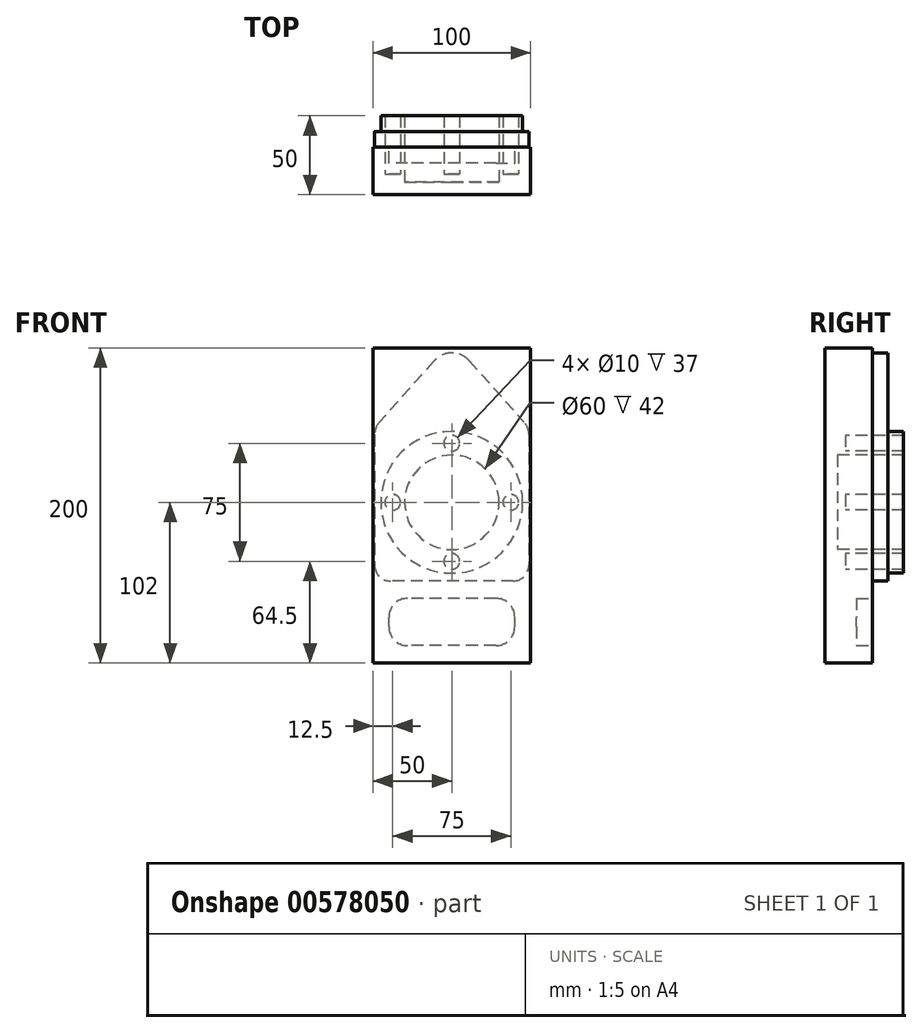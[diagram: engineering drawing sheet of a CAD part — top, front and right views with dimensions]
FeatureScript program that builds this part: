
annotation { "Feature Type Name" : "Feature", "Feature Type Description" : "" }
export const myFeature = defineFeature(function(context is Context, id is Id, definition is map)
    precondition{}
    {
        {
            var Q0;
            Q0=qCreatedBy(makeId("Front.planeOp"),FACE);
            var sketch = newSketch(context, id + "F0", { "sketchPlane" : qUnion([Q0])});
            skLineSegment(sketch, "E0", {"start": v(0, 0) * mm, "end": v(100, 0) * mm});
            skLineSegment(sketch, "E1", {"start": v(100, 0) * mm, "end": v(100, -200) * mm});
            skLineSegment(sketch, "E2", {"start": v(100, -200) * mm, "end": v(0, -200) * mm});
            skLineSegment(sketch, "E3", {"start": v(0, -200) * mm, "end": v(0, 0) * mm});
            skSolve(sketch);
        }
        {
            var Q0;
            Q0=makeQuery(id+"F0.imprint","IMPRINT",FACE,{"disambiguationData":[TD([[makeQuery(id+"F0.imprint","IMPRINT",EDGE,{"derivedFrom":sQuery(id+"F0.wireOp",EDGE,"E0")}),-1.0]])]});
            extrude(context, id + "F1", {"entities" : qUnion([Q0]), "depth" : 30 * mm, "offsetDistance" : 25 * mm});
        }
        {
            var Q0;
            Q0=makeQuery(id+"F1.opExtrude","CAP_FACE",FACE,{"disambiguationData":[OSD([sQuery(id+"F0.wireOp",EDGE,"E0"),sQuery(id+"F0.wireOp",EDGE,"E1"),sQuery(id+"F0.wireOp",EDGE,"E2"),sQuery(id+"F0.wireOp",EDGE,"E3")])],"isStart":true});
            var sketch = newSketch(context, id + "F2", { "sketchPlane" : qUnion([Q0])});
            skLineSegment(sketch, "E4", {"start": v(-50, -200) * mm, "end": v(-50, 0) * mm, "construction": true});
            skArc(sketch, "E5", {"start": v(-50, -3.1) * mm, "mid": v(-56.12, -4.41) * mm, "end": v(-61.18, -8.1) * mm});
            skLineSegment(sketch, "E6", {"start": v(-61.18, -8.1) * mm, "end": v(-95.94, -46.97) * mm});
            skArc(sketch, "E7", {"start": v(-95.94, -46.97) * mm, "mid": v(-98.21, -50.69) * mm, "end": v(-99, -54.97) * mm});
            skLineSegment(sketch, "E8", {"start": v(-99, -54.97) * mm, "end": v(-99, -138) * mm});
            skLineSegment(sketch, "E9", {"start": v(-89, -148) * mm, "end": v(-50, -148) * mm});
            skArc(sketch, "E10", {"start": v(-99, -138) * mm, "mid": v(-96.07, -145.07) * mm, "end": v(-89, -148) * mm});
            skLineSegment(sketch, "E11.MirrorCS", {"start": v(-38.82, -8.1) * mm, "end": v(-4.06, -46.97) * mm});
            skArc(sketch, "E12.MirrorCS", {"start": v(-50, -3.1) * mm, "mid": v(-43.88, -4.41) * mm, "end": v(-38.82, -8.1) * mm});
            skLineSegment(sketch, "E13.MirrorCS", {"start": v(-1, -54.97) * mm, "end": v(-1, -138) * mm});
            skLineSegment(sketch, "E14.MirrorCS", {"start": v(-11, -148) * mm, "end": v(-50, -148) * mm});
            skArc(sketch, "E15.MirrorCS", {"start": v(-4.06, -46.97) * mm, "mid": v(-1.79, -50.69) * mm, "end": v(-1, -54.97) * mm});
            skArc(sketch, "E16.MirrorCS", {"start": v(-1, -138) * mm, "mid": v(-3.93, -145.07) * mm, "end": v(-11, -148) * mm});
            skSolve(sketch);
        }
        {
            var Q0;
            Q0=makeQuery(id+"F2.imprint","IMPRINT",FACE,{"disambiguationData":[TD([[makeQuery(id+"F2.imprint","IMPRINT",EDGE,{"derivedFrom":sQuery(id+"F2.wireOp",EDGE,"E5")}),1.0]])]});
            extrude(context, id + "F3", {"entities" : qUnion([Q0]), "operationType" : NewBodyOperationType.ADD, "depth" : 10 * mm, "offsetDistance" : 25 * mm});
        }
        {
            var Q0;
            Q0=makeQuery(id+"F3.opExtrude","CAP_FACE",FACE,{"disambiguationData":[OSD([sQuery(id+"F2.wireOp",EDGE,"E5"),sQuery(id+"F2.wireOp",EDGE,"E6"),sQuery(id+"F2.wireOp",EDGE,"E7"),sQuery(id+"F2.wireOp",EDGE,"E8"),sQuery(id+"F2.wireOp",EDGE,"E9"),sQuery(id+"F2.wireOp",EDGE,"E10"),sQuery(id+"F2.wireOp",EDGE,"E11.MirrorCS"),sQuery(id+"F2.wireOp",EDGE,"E12.MirrorCS"),sQuery(id+"F2.wireOp",EDGE,"E13.MirrorCS"),sQuery(id+"F2.wireOp",EDGE,"E14.MirrorCS"),sQuery(id+"F2.wireOp",EDGE,"E15.MirrorCS"),sQuery(id+"F2.wireOp",EDGE,"E16.MirrorCS")])],"isStart":false});
            var sketch = newSketch(context, id + "F4", { "sketchPlane" : qUnion([Q0])});
            skCircle(sketch, "E17", {"center": v(-50, -98) * mm, "radius": 30 * mm});
            skCircle(sketch, "E18", {"center": v(-50, -98) * mm, "radius": 45 * mm});
            skLineSegment(sketch, "E19", {"start": v(-50, 0) * mm, "end": v(-50, -201.16) * mm, "construction": true});
            skPoint(sketch, "E19.startSnap0", {"position": v(-50, -3.1) * mm});
            skLineSegment(sketch, "E20", {"start": v(-99, -98) * mm, "end": v(0, -98) * mm, "construction": true});
            skPoint(sketch, "E20.startSnap0", {"position": v(-99, -96.49) * mm});
            skCircle(sketch, "E21", {"center": v(-50, -135.5) * mm, "radius": 5 * mm});
            skCircle(sketch, "E22", {"center": v(-87.5, -98) * mm, "radius": 5 * mm});
            skCircle(sketch, "E23", {"center": v(-50, -60.5) * mm, "radius": 5 * mm});
            skCircle(sketch, "E24", {"center": v(-12.5, -98) * mm, "radius": 5 * mm});
            skSolve(sketch);
        }
        {
            var Q0;
            Q0=makeQuery(id+"F4.imprint","IMPRINT",FACE,{"disambiguationData":[TD([[makeQuery(id+"F4.imprint","IMPRINT",EDGE,{"derivedFrom":sQuery(id+"F4.wireOp",EDGE,"E17")}),-1.0]])]});
            extrude(context, id + "F5", {"entities" : qUnion([Q0]), "operationType" : NewBodyOperationType.ADD, "depth" : 10 * mm, "offsetDistance" : 25 * mm});
        }
        {
            var Q0;
            Q0=makeQuery(id+"F5.boolean.opBoolean","SPLIT",FACE,{"disambiguationData":[TD([makeQuery(id+"F5.opExtrude","SWEPT_FACE",FACE,{"disambiguationData":[OSD([sQuery(id+"F4.wireOp",EDGE,"E21")])]})])],"derivedFrom":makeQuery(id+"F3.opExtrude","CAP_FACE",FACE,{"disambiguationData":[OSD([sQuery(id+"F2.wireOp",EDGE,"E5"),sQuery(id+"F2.wireOp",EDGE,"E6"),sQuery(id+"F2.wireOp",EDGE,"E7"),sQuery(id+"F2.wireOp",EDGE,"E8"),sQuery(id+"F2.wireOp",EDGE,"E9"),sQuery(id+"F2.wireOp",EDGE,"E10"),sQuery(id+"F2.wireOp",EDGE,"E11.MirrorCS"),sQuery(id+"F2.wireOp",EDGE,"E12.MirrorCS"),sQuery(id+"F2.wireOp",EDGE,"E13.MirrorCS"),sQuery(id+"F2.wireOp",EDGE,"E14.MirrorCS"),sQuery(id+"F2.wireOp",EDGE,"E15.MirrorCS"),sQuery(id+"F2.wireOp",EDGE,"E16.MirrorCS")])],"isStart":false})});
            var Q1;
            Q1=makeQuery(id+"F5.boolean.opBoolean","SPLIT",FACE,{"disambiguationData":[TD([makeQuery(id+"F5.opExtrude","SWEPT_FACE",FACE,{"disambiguationData":[OSD([sQuery(id+"F4.wireOp",EDGE,"E22")])]})])],"derivedFrom":makeQuery(id+"F3.opExtrude","CAP_FACE",FACE,{"disambiguationData":[OSD([sQuery(id+"F2.wireOp",EDGE,"E5"),sQuery(id+"F2.wireOp",EDGE,"E6"),sQuery(id+"F2.wireOp",EDGE,"E7"),sQuery(id+"F2.wireOp",EDGE,"E8"),sQuery(id+"F2.wireOp",EDGE,"E9"),sQuery(id+"F2.wireOp",EDGE,"E10"),sQuery(id+"F2.wireOp",EDGE,"E11.MirrorCS"),sQuery(id+"F2.wireOp",EDGE,"E12.MirrorCS"),sQuery(id+"F2.wireOp",EDGE,"E13.MirrorCS"),sQuery(id+"F2.wireOp",EDGE,"E14.MirrorCS"),sQuery(id+"F2.wireOp",EDGE,"E15.MirrorCS"),sQuery(id+"F2.wireOp",EDGE,"E16.MirrorCS")])],"isStart":false})});
            var Q2;
            Q2=makeQuery(id+"F5.boolean.opBoolean","SPLIT",FACE,{"disambiguationData":[TD([makeQuery(id+"F5.opExtrude","SWEPT_FACE",FACE,{"disambiguationData":[OSD([sQuery(id+"F4.wireOp",EDGE,"E23")])]})])],"derivedFrom":makeQuery(id+"F3.opExtrude","CAP_FACE",FACE,{"disambiguationData":[OSD([sQuery(id+"F2.wireOp",EDGE,"E5"),sQuery(id+"F2.wireOp",EDGE,"E6"),sQuery(id+"F2.wireOp",EDGE,"E7"),sQuery(id+"F2.wireOp",EDGE,"E8"),sQuery(id+"F2.wireOp",EDGE,"E9"),sQuery(id+"F2.wireOp",EDGE,"E10"),sQuery(id+"F2.wireOp",EDGE,"E11.MirrorCS"),sQuery(id+"F2.wireOp",EDGE,"E12.MirrorCS"),sQuery(id+"F2.wireOp",EDGE,"E13.MirrorCS"),sQuery(id+"F2.wireOp",EDGE,"E14.MirrorCS"),sQuery(id+"F2.wireOp",EDGE,"E15.MirrorCS"),sQuery(id+"F2.wireOp",EDGE,"E16.MirrorCS")])],"isStart":false})});
            var Q3;
            Q3=makeQuery(id+"F5.boolean.opBoolean","SPLIT",FACE,{"disambiguationData":[TD([makeQuery(id+"F5.opExtrude","SWEPT_FACE",FACE,{"disambiguationData":[OSD([sQuery(id+"F4.wireOp",EDGE,"E24")])]})])],"derivedFrom":makeQuery(id+"F3.opExtrude","CAP_FACE",FACE,{"disambiguationData":[OSD([sQuery(id+"F2.wireOp",EDGE,"E5"),sQuery(id+"F2.wireOp",EDGE,"E6"),sQuery(id+"F2.wireOp",EDGE,"E7"),sQuery(id+"F2.wireOp",EDGE,"E8"),sQuery(id+"F2.wireOp",EDGE,"E9"),sQuery(id+"F2.wireOp",EDGE,"E10"),sQuery(id+"F2.wireOp",EDGE,"E11.MirrorCS"),sQuery(id+"F2.wireOp",EDGE,"E12.MirrorCS"),sQuery(id+"F2.wireOp",EDGE,"E13.MirrorCS"),sQuery(id+"F2.wireOp",EDGE,"E14.MirrorCS"),sQuery(id+"F2.wireOp",EDGE,"E15.MirrorCS"),sQuery(id+"F2.wireOp",EDGE,"E16.MirrorCS")])],"isStart":false})});
            extrude(context, id + "F6", {"entities" : qUnion([Q0, Q1, Q2, Q3]), "operationType" : NewBodyOperationType.REMOVE, "oppositeDirection" : true, "depth" : 27 * mm, "offsetDistance" : 25 * mm});
        }
        {
            var Q0;
            Q0=makeQuery(id+"F5.boolean.opBoolean","SPLIT",FACE,{"disambiguationData":[TD([makeQuery(id+"F5.opExtrude","SWEPT_FACE",FACE,{"disambiguationData":[OSD([sQuery(id+"F4.wireOp",EDGE,"E17")])]})])],"derivedFrom":makeQuery(id+"F3.opExtrude","CAP_FACE",FACE,{"disambiguationData":[OSD([sQuery(id+"F2.wireOp",EDGE,"E5"),sQuery(id+"F2.wireOp",EDGE,"E6"),sQuery(id+"F2.wireOp",EDGE,"E7"),sQuery(id+"F2.wireOp",EDGE,"E8"),sQuery(id+"F2.wireOp",EDGE,"E9"),sQuery(id+"F2.wireOp",EDGE,"E10"),sQuery(id+"F2.wireOp",EDGE,"E11.MirrorCS"),sQuery(id+"F2.wireOp",EDGE,"E12.MirrorCS"),sQuery(id+"F2.wireOp",EDGE,"E13.MirrorCS"),sQuery(id+"F2.wireOp",EDGE,"E14.MirrorCS"),sQuery(id+"F2.wireOp",EDGE,"E15.MirrorCS"),sQuery(id+"F2.wireOp",EDGE,"E16.MirrorCS")])],"isStart":false})});
            extrude(context, id + "F7", {"entities" : qUnion([Q0]), "operationType" : NewBodyOperationType.REMOVE, "oppositeDirection" : true, "depth" : 32 * mm, "offsetDistance" : 25 * mm});
        }
        {
            var Q0;
            Q0=makeQuery(id+"F1.opExtrude","CAP_FACE",FACE,{"disambiguationData":[OSD([sQuery(id+"F0.wireOp",EDGE,"E0"),sQuery(id+"F0.wireOp",EDGE,"E1"),sQuery(id+"F0.wireOp",EDGE,"E2"),sQuery(id+"F0.wireOp",EDGE,"E3")])],"isStart":true});
            var sketch = newSketch(context, id + "F8", { "sketchPlane" : qUnion([Q0])});
            skLineSegment(sketch, "E25", {"start": v(-50, -3.1) * mm, "end": v(-50, -200) * mm, "construction": true});
            skLineSegment(sketch, "E26", {"start": v(-78, -189) * mm, "end": v(-22, -189) * mm});
            skLineSegment(sketch, "E27", {"start": v(-78, -159) * mm, "end": v(-22, -159) * mm});
            skLineSegment(sketch, "E28", {"start": v(-10, -177) * mm, "end": v(-10, -171) * mm});
            skLineSegment(sketch, "E29", {"start": v(-90, -177) * mm, "end": v(-90, -171) * mm});
            skArc(sketch, "E30", {"start": v(-90, -177) * mm, "mid": v(-86.49, -185.49) * mm, "end": v(-78, -189) * mm});
            skArc(sketch, "E31", {"start": v(-78, -159) * mm, "mid": v(-86.49, -162.51) * mm, "end": v(-90, -171) * mm});
            skArc(sketch, "E32", {"start": v(-10, -171) * mm, "mid": v(-13.51, -162.51) * mm, "end": v(-22, -159) * mm});
            skArc(sketch, "E33", {"start": v(-22, -189) * mm, "mid": v(-13.51, -185.49) * mm, "end": v(-10, -177) * mm});
            skSolve(sketch);
        }
        {
            var Q0;
            Q0=makeQuery(id+"F8.imprint","IMPRINT",FACE,{"disambiguationData":[TD([[makeQuery(id+"F8.imprint","IMPRINT",EDGE,{"derivedFrom":sQuery(id+"F8.wireOp",EDGE,"E26")}),1.0]])]});
            extrude(context, id + "F9", {"entities" : qUnion([Q0]), "operationType" : NewBodyOperationType.REMOVE, "oppositeDirection" : true, "depth" : 10 * mm, "offsetDistance" : 25 * mm});
        }
    });
